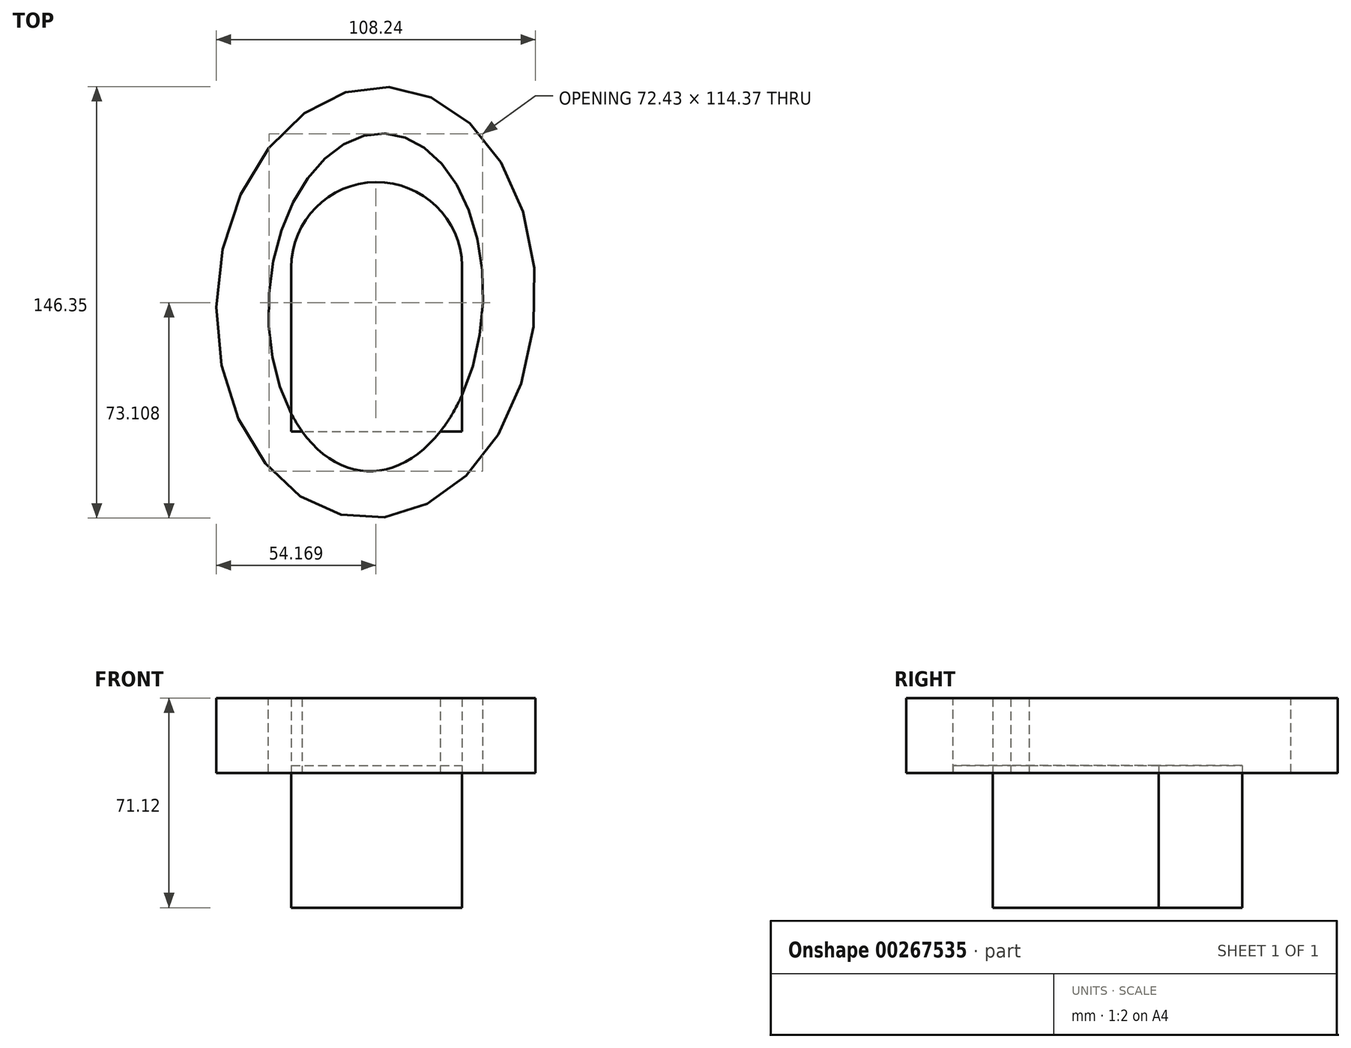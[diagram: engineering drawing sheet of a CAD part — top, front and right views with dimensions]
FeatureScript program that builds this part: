
annotation { "Feature Type Name" : "Feature", "Feature Type Description" : "" }
export const myFeature = defineFeature(function(context is Context, id is Id, definition is map)
    precondition{}
    {
        {
            var Q0;
            Q0=qCreatedBy(makeId("Top.planeOp"),FACE);
            var sketch = newSketch(context, id + "F0", { "sketchPlane" : qUnion([Q0])});
            skLineSegment(sketch, "E0", {"start": v(-32.71, 35.67) * mm, "end": v(-32.71, -19.9) * mm});
            skLineSegment(sketch, "E1", {"start": v(-32.71, -19.9) * mm, "end": v(25.22, -19.9) * mm});
            skLineSegment(sketch, "E2", {"start": v(25.22, -19.9) * mm, "end": v(25.22, 36.26) * mm});
            skArc(sketch, "E3", {"start": v(-32.71, 35.67) * mm, "mid": v(-4.04, 64.64) * mm, "end": v(25.22, 36.26) * mm});
            skSolve(sketch);
        }
        {
            var Q0;
            Q0 = qSketchRegion(id + "F0", true);
            extrude(context, id + "F1", {"entities" : qUnion([Q0]), "depth" : 45.72 * mm});
        }
        {
            var Q0;
            Q0=makeQuery(id+"F1.opExtrude","CAP_FACE",FACE,{"disambiguationData":[OSD([sQuery(id+"F0.wireOp",EDGE,"E0"),sQuery(id+"F0.wireOp",EDGE,"E1"),sQuery(id+"F0.wireOp",EDGE,"E2"),sQuery(id+"F0.wireOp",EDGE,"E3")])],"isStart":false});
            var sketch = newSketch(context, id + "F2", { "sketchPlane" : qUnion([Q0])});
            skEllipse(sketch, "E4", {"center": v(-4.04, 23.85) * mm, "majorRadius": 73.24 * mm, "minorRadius": 54.04 * mm, "majorAxis": v(0.06, 1)});
            skPoint(sketch, "E4.centerSnap0", {"position": v(-4.04, 64.64) * mm});
            skEllipse(sketch, "E5", {"center": v(-4.04, 23.85) * mm, "majorRadius": 57.31 * mm, "minorRadius": 36.3 * mm, "majorAxis": v(0.06, 1)});
            skSolve(sketch);
        }
        {
            var Q0;
            {var subQ5=makeQuery(id+"F1.opExtrude","CAP_EDGE",EDGE,{"disambiguationData":[OSD([sQuery(id+"F0.wireOp",EDGE,"E3")])],"isStart":false});Q0=makeQuery(id+"F2.imprint","IMPRINT",FACE,{"disambiguationData":[TD([[makeQuery(id+"F2.imprint","IMPRINT",EDGE,{"derivedFrom":subQ5}),1.0]])]});}
            var Q1;
            {var subQ0=sQuery(id+"F2.wireOp",EDGE,"E5");var subQ1=makeQuery(id+"F1.opExtrude","CAP_EDGE",EDGE,{"disambiguationData":[OSD([sQuery(id+"F0.wireOp",EDGE,"E1")])],"isStart":false});var subQ2=makeQuery(id+"F2.imprint","INTERSECT",VERTEX,{"disambiguationData":[OD(0.0)],"derivedFrom":[subQ1,subQ0]});Q1=makeQuery(id+"F2.imprint","IMPRINT",FACE,{"disambiguationData":[TD([[makeQuery(id+"F2.imprint","IMPRINT",EDGE,{"disambiguationData":[TD([[subQ2,-1.0]])],"derivedFrom":subQ0}),1.0]])]});}
            extrude(context, id + "F3", {"entities" : qUnion([Q0, Q1]), "depth" : 2.54 * mm});
        }
        {
            var Q0;
            Q0=makeQuery(id+"F2.imprint","IMPRINT",FACE,{"disambiguationData":[TD([[makeQuery(id+"F2.imprint","IMPRINT",EDGE,{"derivedFrom":sQuery(id+"F2.wireOp",EDGE,"E4")}),1.0]])]});
            extrude(context, id + "F4", {"entities" : qUnion([Q0]), "depth" : 25.4 * mm});
        }
    });
